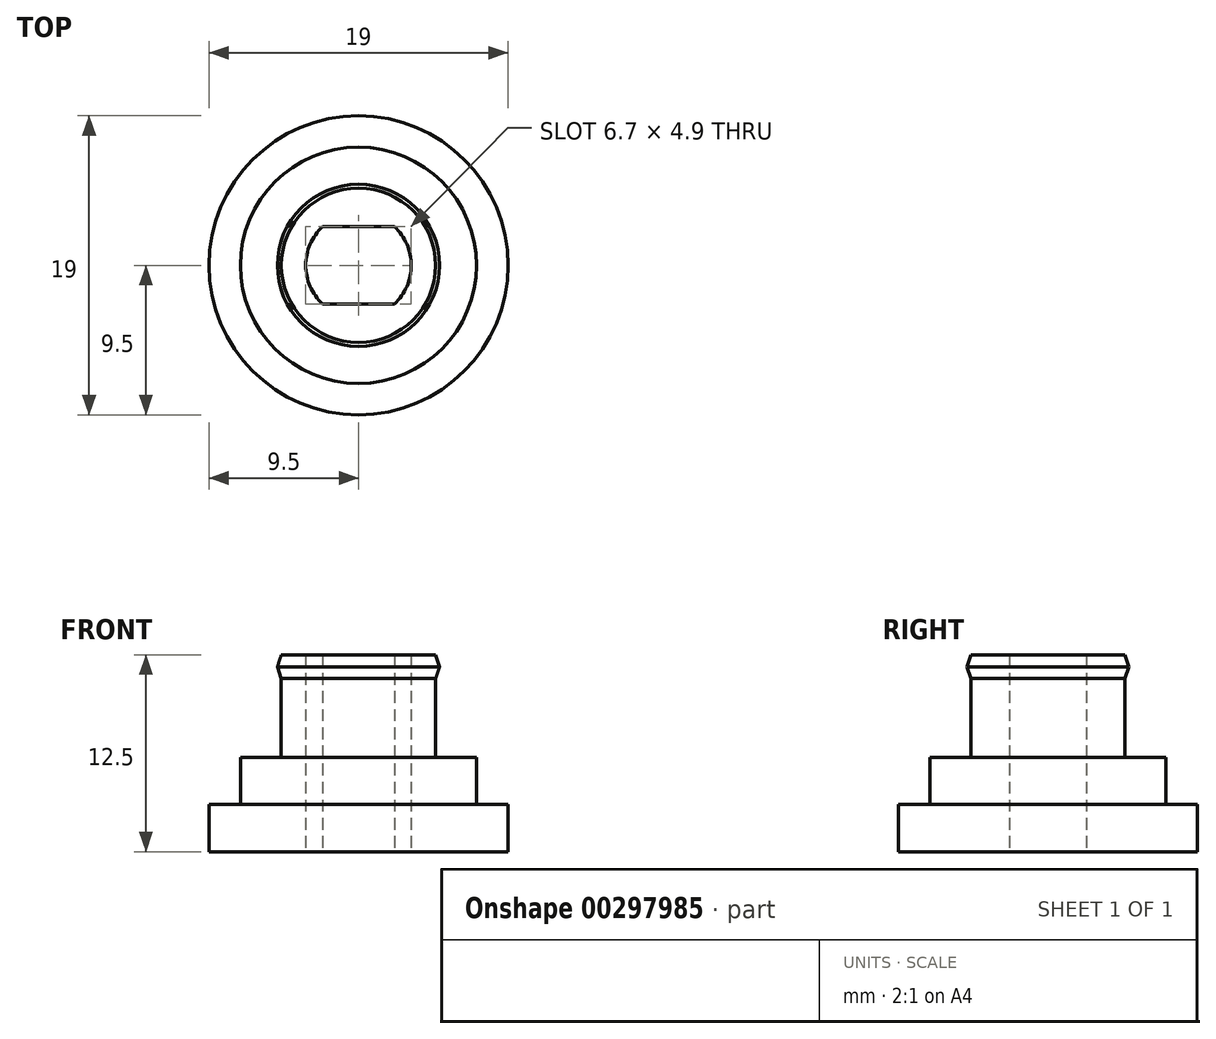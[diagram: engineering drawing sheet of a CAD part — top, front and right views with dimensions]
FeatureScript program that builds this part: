
annotation { "Feature Type Name" : "Feature", "Feature Type Description" : "" }
export const myFeature = defineFeature(function(context is Context, id is Id, definition is map)
    precondition{}
    {
        {
            assignVariable(context, id + "F0", {"name" : "e", "anyValue" : 3});
        }
        {
            assignVariable(context, id + "F1", {"name" : "h1", "anyValue" : 3});
        }
        {
            assignVariable(context, id + "F2", {"name" : "h2", "anyValue" : 6.5});
        }
        {
            var Q0;
            Q0=qCreatedBy(makeId("Top.planeOp"),FACE);
            var sketch = newSketch(context, id + "F3", { "sketchPlane" : qUnion([Q0])});
            skCircle(sketch, "E0", {"center": v(0, 0) * mm, "radius": 9.5 * mm});
            skCircle(sketch, "E1", {"center": v(0, 0) * mm, "radius": 7.5 * mm});
            skCircle(sketch, "E2", {"center": v(0, 0) * mm, "radius": 4.9 * mm});
            skArc(sketch, "E3", {"start": v(-2.28, 2.45) * mm, "mid": v(-3.35, 0) * mm, "end": v(-2.28, -2.45) * mm});
            skLineSegment(sketch, "E4.bottom", {"start": v(2.28, -2.45) * mm, "end": v(-2.28, -2.45) * mm});
            skLineSegment(sketch, "E4.top", {"start": v(2.28, 2.45) * mm, "end": v(-2.28, 2.45) * mm});
            skArc(sketch, "E5.trimOffspring", {"start": v(2.28, -2.45) * mm, "mid": v(3.35, 0) * mm, "end": v(2.28, 2.45) * mm});
            skPoint(sketch, "E6.orphan", {"position": v(3.35, 2.45) * mm});
            skPoint(sketch, "E7.orphan", {"position": v(3.35, -2.45) * mm});
            skPoint(sketch, "E8.orphan", {"position": v(-3.35, -2.45) * mm});
            skPoint(sketch, "E9.orphan", {"position": v(-3.35, 2.45) * mm});
            skSolve(sketch);
        }
        {
            var Q0;
            Q0=makeQuery(id+"F3.imprint","IMPRINT",FACE,{"disambiguationData":[TD([[makeQuery(id+"F3.imprint","IMPRINT",EDGE,{"derivedFrom":sQuery(id+"F3.wireOp",EDGE,"E0")}),1.0]])]});
            var Q1;
            Q1=makeQuery(id+"F3.imprint","IMPRINT",FACE,{"disambiguationData":[TD([[makeQuery(id+"F3.imprint","IMPRINT",EDGE,{"derivedFrom":sQuery(id+"F3.wireOp",EDGE,"E1")}),1.0]])]});
            var Q2;
            Q2=makeQuery(id+"F3.imprint","IMPRINT",FACE,{"disambiguationData":[TD([[makeQuery(id+"F3.imprint","IMPRINT",EDGE,{"derivedFrom":sQuery(id+"F3.wireOp",EDGE,"E2")}),1.0]])]});
            extrude(context, id + "F4", {"entities" : qUnion([Q0, Q1, Q2]), "depth" : (getVariable(context, 'e')) * mm});
        }
        {
            var Q0;
            Q0=makeQuery(id+"F3.imprint","IMPRINT",FACE,{"disambiguationData":[TD([[makeQuery(id+"F3.imprint","IMPRINT",EDGE,{"derivedFrom":sQuery(id+"F3.wireOp",EDGE,"E1")}),1.0]])]});
            var Q1;
            Q1=makeQuery(id+"F3.imprint","IMPRINT",FACE,{"disambiguationData":[TD([[makeQuery(id+"F3.imprint","IMPRINT",EDGE,{"derivedFrom":sQuery(id+"F3.wireOp",EDGE,"E2")}),1.0]])]});
            extrude(context, id + "F5", {"entities" : qUnion([Q0, Q1]), "operationType" : NewBodyOperationType.ADD, "depth" : (getVariable(context, 'e') + getVariable(context, 'h1')) * mm});
        }
        {
            var Q0;
            Q0=makeQuery(id+"F3.imprint","IMPRINT",FACE,{"disambiguationData":[TD([[makeQuery(id+"F3.imprint","IMPRINT",EDGE,{"derivedFrom":sQuery(id+"F3.wireOp",EDGE,"E2")}),1.0]])]});
            extrude(context, id + "F6", {"entities" : qUnion([Q0]), "operationType" : NewBodyOperationType.ADD, "depth" : (getVariable(context, 'e') + getVariable(context, 'h1') + getVariable(context, 'h2')) * mm});
        }
        {
            var Q0;
            Q0=qCreatedBy(makeId("Front.planeOp"),FACE);
            var sketch = newSketch(context, id + "F7", { "sketchPlane" : qUnion([Q0])});
            skLineSegment(sketch, "E10", {"start": v(0, 0) * mm, "end": v(0, 17.5) * mm, "construction": true});
            skLineSegment(sketch, "E11", {"start": v(-4.9, 6) * mm, "end": v(-4.9, 12.5) * mm});
            skLineSegment(sketch, "E12", {"start": v(4.9, 12.5) * mm, "end": v(4.9, 6) * mm});
            skLineSegment(sketch, "E13.bottom", {"start": v(4.9, 12.5) * mm, "end": v(5.15, 12.5) * mm, "construction": true});
            skLineSegment(sketch, "E13.top", {"start": v(4.9, 11) * mm, "end": v(5.15, 11) * mm, "construction": true});
            skLineSegment(sketch, "E13.left", {"start": v(4.9, 12.5) * mm, "end": v(4.9, 11) * mm, "construction": true});
            skLineSegment(sketch, "E13.right", {"start": v(5.15, 12.5) * mm, "end": v(5.15, 11) * mm, "construction": true});
            skPoint(sketch, "E14", {"position": v(5.15, 11.75) * mm});
            skLineSegment(sketch, "E15", {"start": v(4.9, 12.5) * mm, "end": v(5.15, 11.75) * mm});
            skLineSegment(sketch, "E16", {"start": v(5.15, 11.75) * mm, "end": v(4.9, 11) * mm});
            skLineSegment(sketch, "E17", {"start": v(4.9, 11) * mm, "end": v(4.9, 12.5) * mm});
            skSolve(sketch);
        }
        {
            var Q0;
            Q0=makeQuery(id+"F7.imprint","IMPRINT",FACE,{"disambiguationData":[TD([[makeQuery(id+"F7.imprint","IMPRINT",EDGE,{"derivedFrom":sQuery(id+"F7.wireOp",EDGE,"E15")}),-1.0]])]});
            var Q1;
            Q1=sQuery(id+"F7.wireOp",EDGE,"E10");
            revolve(context, id + "F8", {"operationType" : NewBodyOperationType.ADD, "entities" : qUnion([Q0]), "axis" : qUnion([Q1]), "revolveType" : RevolveType.FULL});
        }
        {
            var Q0;
            Q0=makeQuery(id+"F6.opExtrude","CAP_FACE",FACE,{"disambiguationData":[OSD([sQuery(id+"F3.wireOp",EDGE,"E2"),sQuery(id+"F3.wireOp",EDGE,"E3"),sQuery(id+"F3.wireOp",EDGE,"E4.bottom"),sQuery(id+"F3.wireOp",EDGE,"E4.top"),sQuery(id+"F3.wireOp",EDGE,"E5.trimOffspring")])],"isStart":false});
            cPlane(context, id + "F9", {"entities" : qUnion([Q0]), "cplaneType" : CPlaneType.OFFSET, "offset" : 0 * mm, "width" : 150 * mm, "height" : 150 * mm});
        }
    });
